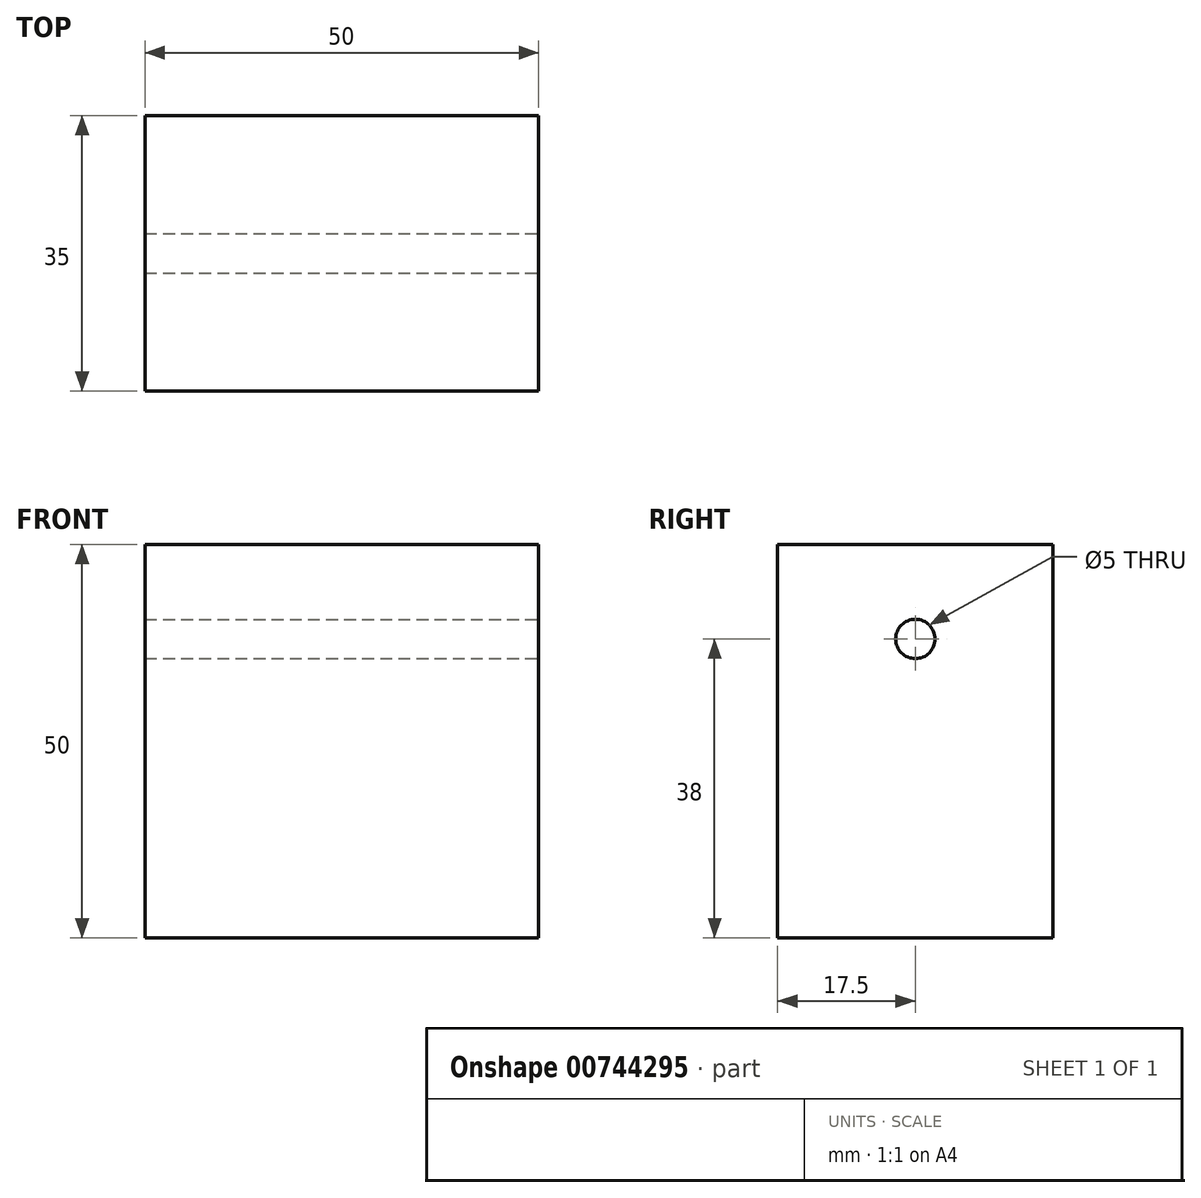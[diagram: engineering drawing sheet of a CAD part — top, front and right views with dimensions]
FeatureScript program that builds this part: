
annotation { "Feature Type Name" : "Feature", "Feature Type Description" : "" }
export const myFeature = defineFeature(function(context is Context, id is Id, definition is map)
    precondition{}
    {
        {
            var Q0;
            Q0=qCreatedBy(makeId("Front.planeOp"),FACE);
            var sketch = newSketch(context, id + "F0", { "sketchPlane" : qUnion([Q0])});
            skLineSegment(sketch, "E0.bottom", {"start": v(-25, 25) * mm, "end": v(25, 25) * mm});
            skLineSegment(sketch, "E0.top", {"start": v(-25, -25) * mm, "end": v(25, -25) * mm});
            skLineSegment(sketch, "E0.left", {"start": v(-25, 25) * mm, "end": v(-25, -25) * mm});
            skLineSegment(sketch, "E0.right", {"start": v(25, 25) * mm, "end": v(25, -25) * mm});
            skSolve(sketch);
        }
        {
            var Q0;
            Q0=makeQuery(id+"F0.imprint","IMPRINT",FACE,{"disambiguationData":[TD([[makeQuery(id+"F0.imprint","IMPRINT",EDGE,{"derivedFrom":sQuery(id+"F0.wireOp",EDGE,"E0.bottom")}),-1.0]])]});
            extrude(context, id + "F1", {"entities" : qUnion([Q0]), "depth" : 35 * mm, "offsetDistance" : 25 * mm});
        }
        {
            var Q0;
            Q0=makeQuery(id+"F1.opExtrude","SWEPT_FACE",FACE,{"disambiguationData":[OSD([sQuery(id+"F0.wireOp",EDGE,"E0.right")])]});
            var sketch = newSketch(context, id + "F2", { "sketchPlane" : qUnion([Q0])});
            skCircle(sketch, "E1", {"center": v(-17.5, 13) * mm, "radius": 2.5 * mm});
            skLineSegment(sketch, "E2", {"start": v(-17.5, 25) * mm, "end": v(-17.5, -37.23) * mm, "construction": true});
            skSolve(sketch);
        }
        {
            var Q0;
            Q0 = qSketchRegion(id + "F2", true);
            extrude(context, id + "F3", {"entities" : qUnion([Q0]), "operationType" : NewBodyOperationType.REMOVE, "endBound" : BoundingType.THROUGH_ALL, "oppositeDirection" : true, "depth" : 25 * mm, "offsetDistance" : 25 * mm});
        }
    });
